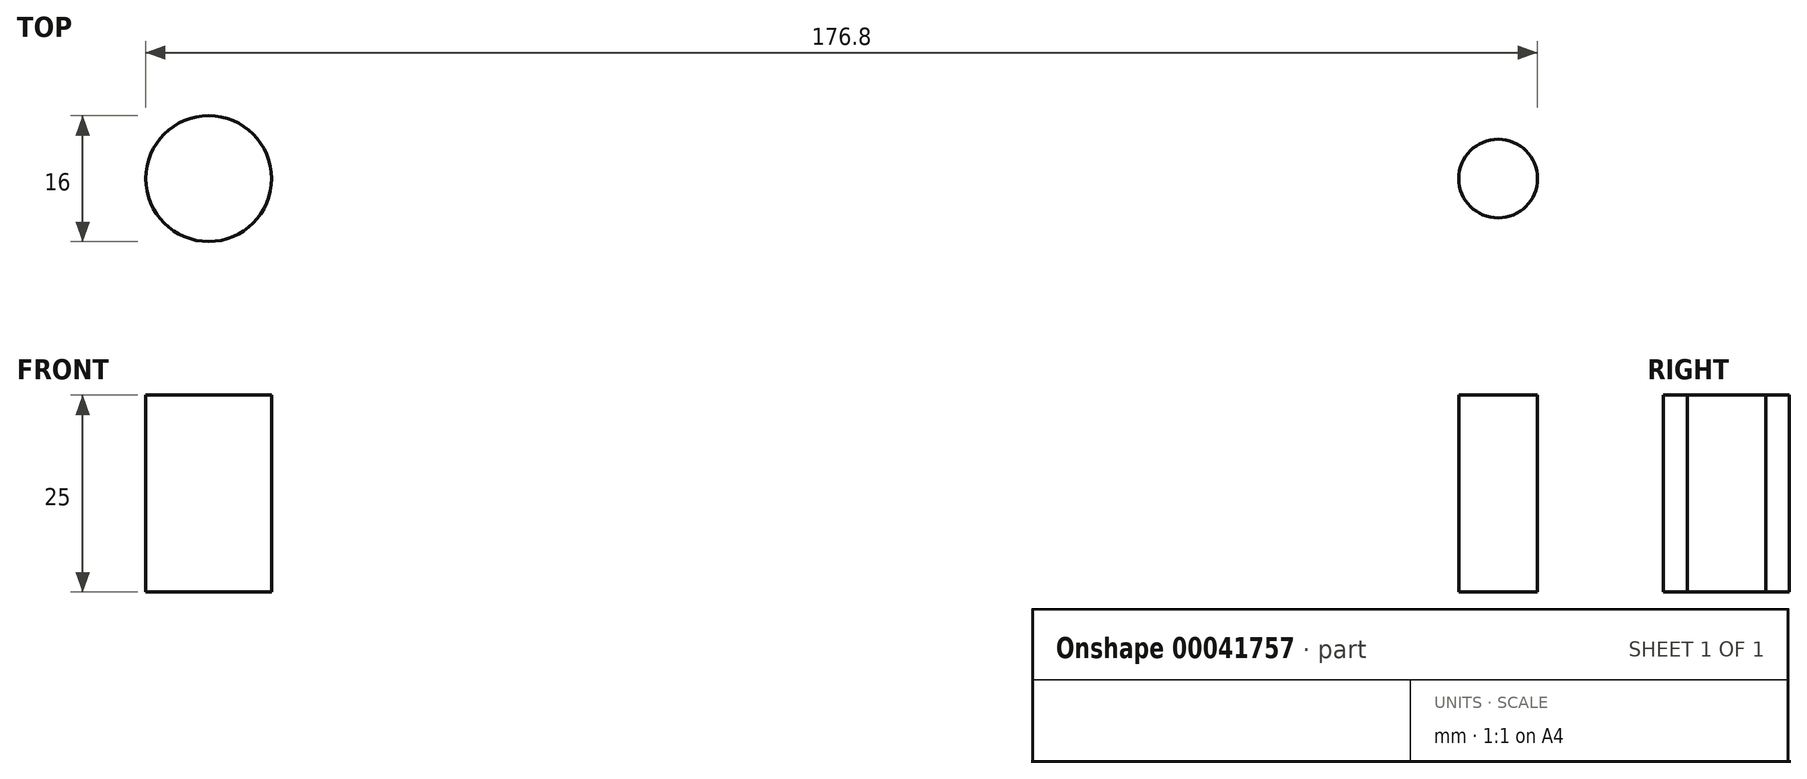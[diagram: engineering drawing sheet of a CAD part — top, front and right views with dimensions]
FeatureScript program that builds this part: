
annotation { "Feature Type Name" : "Feature", "Feature Type Description" : "" }
export const myFeature = defineFeature(function(context is Context, id is Id, definition is map)
    precondition{}
    {
        {
            var Q0;
            Q0=qCreatedBy(makeId("Top.planeOp"),FACE);
            var sketch = newSketch(context, id + "F0", { "sketchPlane" : qUnion([Q0])});
            skCircle(sketch, "E0", {"center": v(0, 0) * mm, "radius": 8 * mm});
            skCircle(sketch, "E1", {"center": v(163.8, 0) * mm, "radius": 5 * mm});
            skSolve(sketch);
        }
        {
            var Q0;
            Q0 = qSketchRegion(id + "F0", true);
            extrude(context, id + "F1", {"entities" : qUnion([Q0]), "depth" : 25 * mm, "symmetric" : true});
        }
    });
